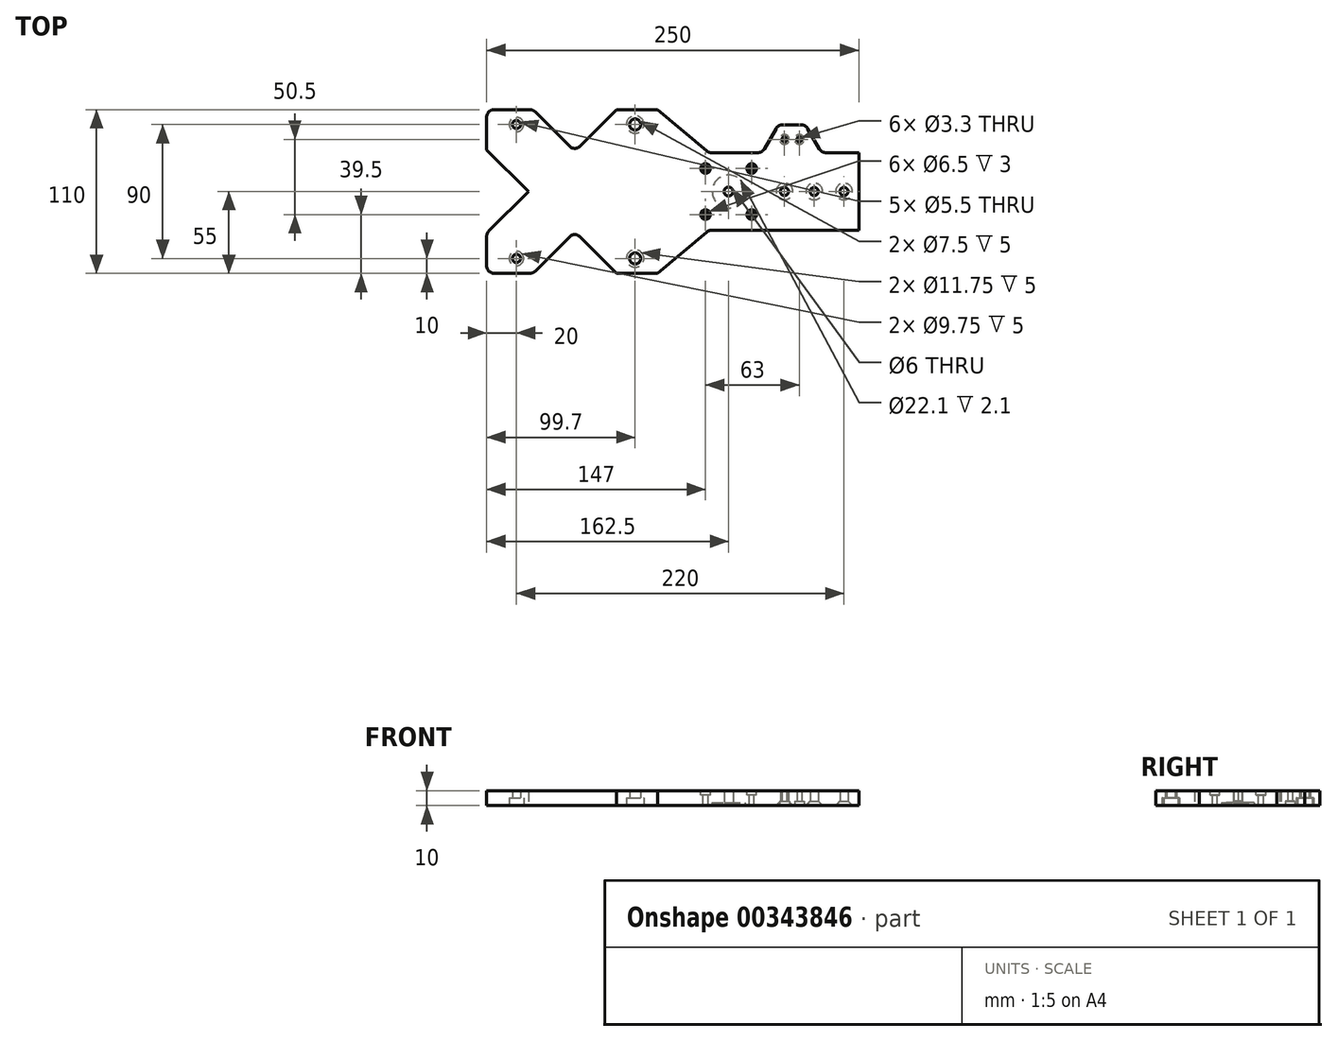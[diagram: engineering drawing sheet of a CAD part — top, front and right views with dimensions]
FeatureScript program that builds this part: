
annotation { "Feature Type Name" : "Feature", "Feature Type Description" : "" }
export const myFeature = defineFeature(function(context is Context, id is Id, definition is map)
    precondition{}
    {
        {
            var Q0;
            Q0=qCreatedBy(makeId("Top.planeOp"),FACE);
            var sketch = newSketch(context, id + "F0", { "sketchPlane" : qUnion([Q0])});
            skLineSegment(sketch, "E0.bottom", {"start": v(125, -55) * mm, "end": v(-125, -55) * mm});
            skLineSegment(sketch, "E0.top", {"start": v(125, 55) * mm, "end": v(-125, 55) * mm});
            skLineSegment(sketch, "E0.left", {"start": v(125, -55) * mm, "end": v(125, 55) * mm});
            skLineSegment(sketch, "E0.right", {"start": v(-125, -55) * mm, "end": v(-125, 55) * mm});
            skPoint(sketch, "E0.middle", {"position": v(0, 0) * mm});
            skCircle(sketch, "E1", {"center": v(-105, 45) * mm, "radius": 2.65 * mm});
            skCircle(sketch, "E2.MirrorC", {"center": v(-105, -45) * mm, "radius": 2.65 * mm});
            skCircle(sketch, "E3", {"center": v(-25.3, 45) * mm, "radius": 3.75 * mm});
            skCircle(sketch, "E4.MirrorC", {"center": v(-25.3, -45) * mm, "radius": 3.75 * mm});
            skCircle(sketch, "E5", {"center": v(115, 0) * mm, "radius": 2.65 * mm});
            skCircle(sketch, "E6", {"center": v(95, 0) * mm, "radius": 2.65 * mm});
            skCircle(sketch, "E7", {"center": v(75, 0) * mm, "radius": 2.65 * mm});
            skLineSegment(sketch, "E8", {"start": v(0, 0) * mm, "end": v(75, 0) * mm, "construction": true});
            skCircle(sketch, "E9", {"center": v(37.5, 0) * mm, "radius": 11.1 * mm, "construction": true});
            skLineSegment(sketch, "E10", {"start": v(37.5, 0) * mm, "end": v(22, -15.5) * mm, "construction": true});
            skLineSegment(sketch, "E11.MirrorCS", {"start": v(37.5, 0) * mm, "end": v(22, 15.5) * mm, "construction": true});
            skLineSegment(sketch, "E12", {"start": v(37.5, 38.01) * mm, "end": v(37.5, 0) * mm, "construction": true});
            skLineSegment(sketch, "E13.MirrorCS", {"start": v(37.5, 0) * mm, "end": v(53, -15.5) * mm, "construction": true});
            skLineSegment(sketch, "E14.MirrorCS", {"start": v(37.5, 0) * mm, "end": v(53, 15.5) * mm, "construction": true});
            skCircle(sketch, "E15", {"center": v(22, -15.5) * mm, "radius": 1.6 * mm});
            skCircle(sketch, "E16.MirrorC", {"center": v(53, -15.5) * mm, "radius": 1.6 * mm});
            skCircle(sketch, "E17.MirrorC", {"center": v(22, 15.5) * mm, "radius": 1.6 * mm});
            skCircle(sketch, "E18.MirrorC", {"center": v(53, 15.5) * mm, "radius": 1.6 * mm});
            skCircle(sketch, "E19", {"center": v(37.5, 0) * mm, "radius": 3 * mm});
            skLineSegment(sketch, "E20", {"start": v(-125, -28) * mm, "end": v(-97, 0) * mm});
            skLineSegment(sketch, "E21.MirrorCS", {"start": v(-125, 28) * mm, "end": v(-97, 0) * mm});
            skLineSegment(sketch, "E22", {"start": v(-125, 28) * mm, "end": v(-125, -28) * mm});
            skCircle(sketch, "E23", {"center": v(75, 35) * mm, "radius": 1.6 * mm});
            skCircle(sketch, "E24", {"center": v(85, 35) * mm, "radius": 1.6 * mm});
            skLineSegment(sketch, "E25", {"start": v(75, 35) * mm, "end": v(79.22, 35) * mm, "construction": true});
            skLineSegment(sketch, "E26", {"start": v(75, 68.62) * mm, "end": v(75, -17.42) * mm, "construction": true});
            skSolve(sketch);
        }
        {
            var Q0;
            Q0=qSketchRegion(id+"F0",true);
            extrude(context, id + "F1", {"entities" : qUnion([Q0]), "depth" : 10 * mm});
        }
        {
            var Q0;
            Q0=sQuery(id+"F0.wireOp",VERTEX,"E7.center");
            var Q1;
            Q1=sQuery(id+"F0.wireOp",VERTEX,"E6.center");
            var Q2;
            Q2=sQuery(id+"F0.wireOp",VERTEX,"E5.center");
            var Q3;
            Q3=makeQuery(id+"F1.opExtrude","SWEPT_BODY",BODY,{"disambiguationData":[OSD([sQuery(id+"F0.wireOp",EDGE,"E0.bottom"),sQuery(id+"F0.wireOp",EDGE,"E0.top"),sQuery(id+"F0.wireOp",EDGE,"E0.left"),sQuery(id+"F0.wireOp",EDGE,"E0.right"),sQuery(id+"F0.wireOp",EDGE,"E1"),sQuery(id+"F0.wireOp",EDGE,"E2.MirrorC"),sQuery(id+"F0.wireOp",EDGE,"E3"),sQuery(id+"F0.wireOp",EDGE,"E4.MirrorC"),sQuery(id+"F0.wireOp",EDGE,"E5"),sQuery(id+"F0.wireOp",EDGE,"E6"),sQuery(id+"F0.wireOp",EDGE,"E7")])]});
            hole(context, id + "F2", {"style" : HoleStyle.C_SINK, "endStyle" : HoleEndStyle.THROUGH, "oppositeDirection" : true, "standardTappedOrClearance" : lookupTablePath({ "standard" : "ISO", "fit" : "Normal", "size" : "M5", "type" : "Clearance" }), "standardBlindInLast" : lookupTablePath({ "fit" : "Standard", "standard" : "ISO", "size" : "M5", "type" : "Clearance" }), "holeDiameter" : 5.5 * mm, "cSinkDiameter" : 11.2 * mm, "cSinkAngle" : 90 * degree, "isTappedThrough" : true, "tappedDepth" : 12 * mm, "tapClearance" : 3, "locations" : qUnion([Q0, Q1, Q2]), "scope" : qUnion([Q3])});
        }
        {
            var Q0;
            Q0=sQuery(id+"F0.wireOp",VERTEX,"E14.MirrorCS.start");
            var Q1;
            Q1=makeQuery(id+"F1.opExtrude","SWEPT_BODY",BODY,{"disambiguationData":[OSD([sQuery(id+"F0.wireOp",EDGE,"E0.bottom"),sQuery(id+"F0.wireOp",EDGE,"E0.top"),sQuery(id+"F0.wireOp",EDGE,"E0.left"),sQuery(id+"F0.wireOp",EDGE,"E0.right"),sQuery(id+"F0.wireOp",EDGE,"E1"),sQuery(id+"F0.wireOp",EDGE,"E2.MirrorC"),sQuery(id+"F0.wireOp",EDGE,"E3"),sQuery(id+"F0.wireOp",EDGE,"E4.MirrorC"),sQuery(id+"F0.wireOp",EDGE,"E5"),sQuery(id+"F0.wireOp",EDGE,"E6"),sQuery(id+"F0.wireOp",EDGE,"E7"),sQuery(id+"F0.wireOp",EDGE,"E15"),sQuery(id+"F0.wireOp",EDGE,"E16.MirrorC"),sQuery(id+"F0.wireOp",EDGE,"E17.MirrorC"),sQuery(id+"F0.wireOp",EDGE,"E18.MirrorC"),sQuery(id+"F0.wireOp",EDGE,"E19")])]});
            hole(context, id + "F3", {"style" : HoleStyle.C_BORE, "endStyle" : HoleEndStyle.THROUGH, "oppositeDirection" : true, "holeDiameter" : 5.5 * mm, "cBoreDiameter" : 22.1 * mm, "cBoreDepth" : 2.1 * mm, "isTappedThrough" : true, "tappedDepth" : 12 * mm, "tapClearance" : 3, "locations" : qUnion([Q0]), "scope" : qUnion([Q1])});
        }
        {
            var Q0;
            Q0=makeQuery(id+"F0.imprint","IMPRINT",FACE,{"disambiguationData":[TD([[makeQuery(id+"F0.imprint","IMPRINT",EDGE,{"derivedFrom":sQuery(id+"F0.wireOp",EDGE,"E20")}),1.0]])]});
            extrude(context, id + "F4", {"entities" : qUnion([Q0]), "operationType" : NewBodyOperationType.REMOVE, "endBound" : BoundingType.THROUGH_ALL, "depth" : 25 * mm});
        }
        {
            var Q0;
            Q0=sQuery(id+"F0.wireOp",VERTEX,"E23.center");
            var Q1;
            Q1=sQuery(id+"F0.wireOp",VERTEX,"E24.center");
            var Q2;
            Q2=makeQuery(id+"F1.opExtrude","SWEPT_BODY",BODY,{"disambiguationData":[OSD([sQuery(id+"F0.wireOp",EDGE,"E0.bottom"),sQuery(id+"F0.wireOp",EDGE,"E0.top"),sQuery(id+"F0.wireOp",EDGE,"E0.left"),sQuery(id+"F0.wireOp",EDGE,"E0.right"),sQuery(id+"F0.wireOp",EDGE,"E1"),sQuery(id+"F0.wireOp",EDGE,"E2.MirrorC"),sQuery(id+"F0.wireOp",EDGE,"E3"),sQuery(id+"F0.wireOp",EDGE,"E4.MirrorC"),sQuery(id+"F0.wireOp",EDGE,"E5"),sQuery(id+"F0.wireOp",EDGE,"E6"),sQuery(id+"F0.wireOp",EDGE,"E7"),sQuery(id+"F0.wireOp",EDGE,"E15"),sQuery(id+"F0.wireOp",EDGE,"E16.MirrorC"),sQuery(id+"F0.wireOp",EDGE,"E17.MirrorC"),sQuery(id+"F0.wireOp",EDGE,"E18.MirrorC"),sQuery(id+"F0.wireOp",EDGE,"E19"),sQuery(id+"F0.wireOp",EDGE,"E22")])]});
            hole(context, id + "F5", {"style" : HoleStyle.C_BORE, "endStyle" : HoleEndStyle.THROUGH, "oppositeDirection" : true, "standardTappedOrClearance" : lookupTablePath({ "standard" : "ISO", "fit" : "Normal", "size" : "M3", "type" : "Clearance" }), "standardBlindInLast" : lookupTablePath({ "fit" : "Standard", "standard" : "ISO", "size" : "M3", "type" : "Clearance" }), "holeDiameter" : 3.3 * mm, "cBoreDiameter" : 6.5 * mm, "cBoreDepth" : 3 * mm, "isTappedThrough" : true, "tappedDepth" : 12 * mm, "tapClearance" : 3, "locations" : qUnion([Q0, Q1]), "scope" : qUnion([Q2])});
        }
        {
            var Q0;
            Q0=sQuery(id+"F0.wireOp",VERTEX,"E4.MirrorC.center");
            var Q1;
            Q1=sQuery(id+"F0.wireOp",VERTEX,"E3.center");
            var Q2;
            Q2=makeQuery(id+"F1.opExtrude","SWEPT_BODY",BODY,{"disambiguationData":[OSD([sQuery(id+"F0.wireOp",EDGE,"E0.bottom"),sQuery(id+"F0.wireOp",EDGE,"E0.top"),sQuery(id+"F0.wireOp",EDGE,"E0.left"),sQuery(id+"F0.wireOp",EDGE,"E0.right"),sQuery(id+"F0.wireOp",EDGE,"E1"),sQuery(id+"F0.wireOp",EDGE,"E2.MirrorC"),sQuery(id+"F0.wireOp",EDGE,"E3"),sQuery(id+"F0.wireOp",EDGE,"E4.MirrorC"),sQuery(id+"F0.wireOp",EDGE,"E5"),sQuery(id+"F0.wireOp",EDGE,"E6"),sQuery(id+"F0.wireOp",EDGE,"E7"),sQuery(id+"F0.wireOp",EDGE,"E15"),sQuery(id+"F0.wireOp",EDGE,"E16.MirrorC"),sQuery(id+"F0.wireOp",EDGE,"E17.MirrorC"),sQuery(id+"F0.wireOp",EDGE,"E18.MirrorC"),sQuery(id+"F0.wireOp",EDGE,"E19"),sQuery(id+"F0.wireOp",EDGE,"E22")])]});
            hole(context, id + "F6", {"style" : HoleStyle.C_BORE, "endStyle" : HoleEndStyle.THROUGH, "oppositeDirection" : true, "holeDiameter" : 7.5 * mm, "cBoreDiameter" : 11.75 * mm, "cBoreDepth" : 5 * mm, "isTappedThrough" : true, "tappedDepth" : 12 * mm, "tapClearance" : 3, "locations" : qUnion([Q0, Q1]), "scope" : qUnion([Q2])});
        }
        {
            var Q0;
            Q0=makeQuery(id+"F1.opExtrude","CAP_FACE",FACE,{"disambiguationData":[OSD([sQuery(id+"F0.wireOp",EDGE,"E0.bottom"),sQuery(id+"F0.wireOp",EDGE,"E0.top"),sQuery(id+"F0.wireOp",EDGE,"E0.left"),sQuery(id+"F0.wireOp",EDGE,"E0.right"),sQuery(id+"F0.wireOp",EDGE,"E1"),sQuery(id+"F0.wireOp",EDGE,"E2.MirrorC"),sQuery(id+"F0.wireOp",EDGE,"E3"),sQuery(id+"F0.wireOp",EDGE,"E4.MirrorC"),sQuery(id+"F0.wireOp",EDGE,"E5"),sQuery(id+"F0.wireOp",EDGE,"E6"),sQuery(id+"F0.wireOp",EDGE,"E7"),sQuery(id+"F0.wireOp",EDGE,"E15"),sQuery(id+"F0.wireOp",EDGE,"E16.MirrorC"),sQuery(id+"F0.wireOp",EDGE,"E17.MirrorC"),sQuery(id+"F0.wireOp",EDGE,"E18.MirrorC"),sQuery(id+"F0.wireOp",EDGE,"E19"),sQuery(id+"F0.wireOp",EDGE,"E22"),sQuery(id+"F0.wireOp",EDGE,"E23"),sQuery(id+"F0.wireOp",EDGE,"E24")])],"isStart":false});
            cPlane(context, id + "F7", {"entities" : qUnion([Q0]), "cplaneType" : CPlaneType.OFFSET, "offset" : 0 * mm, "width" : 150 * mm, "height" : 150 * mm});
        }
        {
            var Q0;
            Q0=qCreatedBy(id+"F7.planeOp",FACE);
            var sketch = newSketch(context, id + "F8", { "sketchPlane" : qUnion([Q0])});
            skCircle(sketch, "E27.0", {"center": v(22, 15.5) * mm, "radius": 1.6 * mm, "construction": true});
            skCircle(sketch, "E27.1", {"center": v(53, 15.5) * mm, "radius": 1.6 * mm, "construction": true});
            skCircle(sketch, "E27.2", {"center": v(53, -15.5) * mm, "radius": 1.6 * mm, "construction": true});
            skCircle(sketch, "E27.3", {"center": v(22, -15.5) * mm, "radius": 1.6 * mm, "construction": true});
            skSolve(sketch);
        }
        {
            var Q0;
            Q0=sQuery(id+"F8.wireOp",VERTEX,"E27.1.center");
            var Q1;
            Q1=sQuery(id+"F8.wireOp",VERTEX,"E27.2.center");
            var Q2;
            Q2=sQuery(id+"F8.wireOp",VERTEX,"E27.3.center");
            var Q3;
            Q3=sQuery(id+"F8.wireOp",VERTEX,"E27.0.center");
            var Q4;
            Q4=makeQuery(id+"F1.opExtrude","SWEPT_BODY",BODY,{"disambiguationData":[OSD([sQuery(id+"F0.wireOp",EDGE,"E0.bottom"),sQuery(id+"F0.wireOp",EDGE,"E0.top"),sQuery(id+"F0.wireOp",EDGE,"E0.left"),sQuery(id+"F0.wireOp",EDGE,"E0.right"),sQuery(id+"F0.wireOp",EDGE,"E1"),sQuery(id+"F0.wireOp",EDGE,"E2.MirrorC"),sQuery(id+"F0.wireOp",EDGE,"E3"),sQuery(id+"F0.wireOp",EDGE,"E4.MirrorC"),sQuery(id+"F0.wireOp",EDGE,"E5"),sQuery(id+"F0.wireOp",EDGE,"E6"),sQuery(id+"F0.wireOp",EDGE,"E7"),sQuery(id+"F0.wireOp",EDGE,"E15"),sQuery(id+"F0.wireOp",EDGE,"E16.MirrorC"),sQuery(id+"F0.wireOp",EDGE,"E17.MirrorC"),sQuery(id+"F0.wireOp",EDGE,"E18.MirrorC"),sQuery(id+"F0.wireOp",EDGE,"E19"),sQuery(id+"F0.wireOp",EDGE,"E22"),sQuery(id+"F0.wireOp",EDGE,"E23"),sQuery(id+"F0.wireOp",EDGE,"E24")])]});
            hole(context, id + "F9", {"style" : HoleStyle.C_BORE, "endStyle" : HoleEndStyle.THROUGH, "standardTappedOrClearance" : lookupTablePath({ "standard" : "ISO", "fit" : "Normal", "size" : "M3", "type" : "Clearance" }), "standardBlindInLast" : lookupTablePath({ "fit" : "Standard", "standard" : "ISO", "size" : "M3", "type" : "Clearance" }), "holeDiameter" : 3.3 * mm, "cBoreDiameter" : 6.5 * mm, "cBoreDepth" : 3 * mm, "isTappedThrough" : true, "tappedDepth" : 12 * mm, "tapClearance" : 3, "locations" : qUnion([Q0, Q1, Q2, Q3]), "scope" : qUnion([Q4])});
        }
        {
            var Q0;
            Q0=sQuery(id+"F0.wireOp",VERTEX,"E2.MirrorC.center");
            var Q1;
            Q1=sQuery(id+"F0.wireOp",VERTEX,"E1.center");
            var Q2;
            Q2=makeQuery(id+"F1.opExtrude","SWEPT_BODY",BODY,{"disambiguationData":[OSD([sQuery(id+"F0.wireOp",EDGE,"E0.bottom"),sQuery(id+"F0.wireOp",EDGE,"E0.top"),sQuery(id+"F0.wireOp",EDGE,"E0.left"),sQuery(id+"F0.wireOp",EDGE,"E0.right"),sQuery(id+"F0.wireOp",EDGE,"E1"),sQuery(id+"F0.wireOp",EDGE,"E2.MirrorC"),sQuery(id+"F0.wireOp",EDGE,"E3"),sQuery(id+"F0.wireOp",EDGE,"E4.MirrorC"),sQuery(id+"F0.wireOp",EDGE,"E5"),sQuery(id+"F0.wireOp",EDGE,"E6"),sQuery(id+"F0.wireOp",EDGE,"E7"),sQuery(id+"F0.wireOp",EDGE,"E15"),sQuery(id+"F0.wireOp",EDGE,"E16.MirrorC"),sQuery(id+"F0.wireOp",EDGE,"E17.MirrorC"),sQuery(id+"F0.wireOp",EDGE,"E18.MirrorC"),sQuery(id+"F0.wireOp",EDGE,"E19"),sQuery(id+"F0.wireOp",EDGE,"E22"),sQuery(id+"F0.wireOp",EDGE,"E23"),sQuery(id+"F0.wireOp",EDGE,"E24")])]});
            hole(context, id + "F10", {"style" : HoleStyle.C_BORE, "endStyle" : HoleEndStyle.THROUGH, "oppositeDirection" : true, "standardTappedOrClearance" : lookupTablePath({ "standard" : "ISO", "fit" : "Normal", "size" : "M5", "type" : "Clearance" }), "standardBlindInLast" : lookupTablePath({ "fit" : "Standard", "standard" : "ISO", "size" : "M5", "type" : "Clearance" }), "holeDiameter" : 5.5 * mm, "cBoreDiameter" : 9.75 * mm, "cBoreDepth" : 5 * mm, "isTappedThrough" : true, "tappedDepth" : 12 * mm, "tapClearance" : 3, "locations" : qUnion([Q0, Q1]), "scope" : qUnion([Q2])});
        }
        {
            var Q0;
            Q0=qCreatedBy(id+"F7.planeOp",FACE);
            var sketch = newSketch(context, id + "F11", { "sketchPlane" : qUnion([Q0])});
            skLineSegment(sketch, "E28.0.0", {"start": v(-125, 55) * mm, "end": v(-125, 28) * mm});
            skLineSegment(sketch, "E28.0.1", {"start": v(-125, 28) * mm, "end": v(-97, 0) * mm});
            skLineSegment(sketch, "E28.0.2", {"start": v(-97, 0) * mm, "end": v(-125, -28) * mm});
            skLineSegment(sketch, "E28.0.3", {"start": v(-125, -28) * mm, "end": v(-125, -55) * mm});
            skLineSegment(sketch, "E28.0.4", {"start": v(-125, -55) * mm, "end": v(125, -55) * mm});
            skLineSegment(sketch, "E28.0.5", {"start": v(125, -55) * mm, "end": v(125, 55) * mm});
            skLineSegment(sketch, "E28.0.6", {"start": v(125, 55) * mm, "end": v(-125, 55) * mm});
            skLineSegment(sketch, "E29", {"start": v(-10.3, -55) * mm, "end": v(24.17, -26.07) * mm});
            skLineSegment(sketch, "E30", {"start": v(24.17, -26.07) * mm, "end": v(125, -26.07) * mm});
            skLineSegment(sketch, "E31.MirrorCS", {"start": v(-10.3, 55) * mm, "end": v(24.17, 26.07) * mm});
            skLineSegment(sketch, "E32.MirrorCS", {"start": v(24.17, 26.07) * mm, "end": v(125, 26.07) * mm});
            skLineSegment(sketch, "E33", {"start": v(60, 26.07) * mm, "end": v(70.83, 44.83) * mm});
            skLineSegment(sketch, "E34", {"start": v(70.83, 44.83) * mm, "end": v(89.17, 44.83) * mm});
            skLineSegment(sketch, "E35", {"start": v(89.17, 44.83) * mm, "end": v(100, 26.07) * mm});
            skLineSegment(sketch, "E36", {"start": v(-93.96, -55) * mm, "end": v(-65.86, -26.9) * mm});
            skLineSegment(sketch, "E37", {"start": v(-65.86, -26.9) * mm, "end": v(-37.75, -55) * mm});
            skLineSegment(sketch, "E38", {"start": v(-97, 0) * mm, "end": v(0, 0) * mm, "construction": true});
            skLineSegment(sketch, "E39.MirrorCS", {"start": v(-65.86, 26.9) * mm, "end": v(-37.75, 55) * mm});
            skLineSegment(sketch, "E40.MirrorCS", {"start": v(-93.96, 55) * mm, "end": v(-65.86, 26.9) * mm});
            skSolve(sketch);
        }
        {
            var Q0;
            {var subQ1=sQuery(id+"F11.wireOp",EDGE,"E31.MirrorCS");Q0=makeQuery(id+"F11.imprint","IMPRINT",FACE,{"disambiguationData":[TD([[makeQuery(id+"F11.imprint","IMPRINT",EDGE,{"derivedFrom":subQ1}),1.0]])]});}
            var Q1;
            {var subQ3=sQuery(id+"F11.wireOp",EDGE,"E29");Q1=makeQuery(id+"F11.imprint","IMPRINT",FACE,{"disambiguationData":[TD([[makeQuery(id+"F11.imprint","IMPRINT",EDGE,{"derivedFrom":subQ3}),-1.0]])]});}
            var Q2;
            {var subQ0=sQuery(id+"F11.wireOp",EDGE,"E36");Q2=makeQuery(id+"F11.imprint","IMPRINT",FACE,{"disambiguationData":[TD([[makeQuery(id+"F11.imprint","IMPRINT",EDGE,{"derivedFrom":subQ0}),-1.0]])]});}
            var Q3;
            {var subQ0=sQuery(id+"F11.wireOp",EDGE,"E39.MirrorCS");Q3=makeQuery(id+"F11.imprint","IMPRINT",FACE,{"disambiguationData":[TD([[makeQuery(id+"F11.imprint","IMPRINT",EDGE,{"derivedFrom":subQ0}),1.0]])]});}
            extrude(context, id + "F12", {"entities" : qUnion([Q0, Q1, Q2, Q3]), "operationType" : NewBodyOperationType.REMOVE, "oppositeDirection" : true, "depth" : 25 * mm, "offsetDistance" : 25 * mm});
        }
        {
            var Q0;
            Q0=makeQuery(id+"F4.boolean.opBoolean","COPY",EDGE,{"derivedFrom":makeQuery(id+"F4.opExtrude","SWEPT_EDGE",EDGE,{"disambiguationData":[OSD([sQuery(id+"F0.wireOp",EDGE,"E0.right"),sQuery(id+"F0.wireOp",EDGE,"E20"),sQuery(id+"F0.wireOp",EDGE,"E22")])]})});
            var Q1;
            Q1=makeQuery(id+"F1.opExtrude","SWEPT_EDGE",EDGE,{"disambiguationData":[OSD([sQuery(id+"F0.wireOp",EDGE,"E0.bottom"),sQuery(id+"F0.wireOp",EDGE,"E0.right")])]});
            var Q2;
            Q2=makeQuery(id+"F4.boolean.opBoolean","COPY",EDGE,{"derivedFrom":makeQuery(id+"F4.opExtrude","SWEPT_EDGE",EDGE,{"disambiguationData":[OSD([sQuery(id+"F0.wireOp",EDGE,"E0.right"),sQuery(id+"F0.wireOp",EDGE,"E21.MirrorCS"),sQuery(id+"F0.wireOp",EDGE,"E22")])]})});
            var Q3;
            Q3=makeQuery(id+"F1.opExtrude","SWEPT_EDGE",EDGE,{"disambiguationData":[OSD([sQuery(id+"F0.wireOp",EDGE,"E0.top"),sQuery(id+"F0.wireOp",EDGE,"E0.right")])]});
            var Q4;
            Q4=makeQuery(id+"F12.boolean.opBoolean","COPY",EDGE,{"derivedFrom":makeQuery(id+"F12.opExtrude","SWEPT_EDGE",EDGE,{"disambiguationData":[OSD([sQuery(id+"F11.wireOp",EDGE,"E29"),sQuery(id+"F11.wireOp",EDGE,"E30")])]})});
            var Q5;
            Q5=makeQuery(id+"F12.boolean.opBoolean","COPY",EDGE,{"derivedFrom":makeQuery(id+"F12.opExtrude","SWEPT_EDGE",EDGE,{"disambiguationData":[OSD([sQuery(id+"F11.wireOp",EDGE,"E28.0.4"),sQuery(id+"F11.wireOp",EDGE,"E29")])]})});
            var Q6;
            Q6=makeQuery(id+"F12.boolean.opBoolean","COPY",EDGE,{"derivedFrom":makeQuery(id+"F12.opExtrude","SWEPT_EDGE",EDGE,{"disambiguationData":[OSD([sQuery(id+"F11.wireOp",EDGE,"E28.0.5"),sQuery(id+"F11.wireOp",EDGE,"E30")])]})});
            var Q7;
            Q7=makeQuery(id+"F12.boolean.opBoolean","COPY",EDGE,{"derivedFrom":makeQuery(id+"F12.opExtrude","SWEPT_EDGE",EDGE,{"disambiguationData":[OSD([sQuery(id+"F11.wireOp",EDGE,"E28.0.5"),sQuery(id+"F11.wireOp",EDGE,"E32.MirrorCS")])]})});
            var Q8;
            Q8=makeQuery(id+"F12.boolean.opBoolean","COPY",EDGE,{"derivedFrom":makeQuery(id+"F12.opExtrude","SWEPT_EDGE",EDGE,{"disambiguationData":[OSD([sQuery(id+"F11.wireOp",EDGE,"E32.MirrorCS"),sQuery(id+"F11.wireOp",EDGE,"E35")])]})});
            var Q9;
            Q9=makeQuery(id+"F12.boolean.opBoolean","COPY",EDGE,{"derivedFrom":makeQuery(id+"F12.opExtrude","SWEPT_EDGE",EDGE,{"disambiguationData":[OSD([sQuery(id+"F11.wireOp",EDGE,"E34"),sQuery(id+"F11.wireOp",EDGE,"E35")])]})});
            var Q10;
            Q10=makeQuery(id+"F12.boolean.opBoolean","COPY",EDGE,{"derivedFrom":makeQuery(id+"F12.opExtrude","SWEPT_EDGE",EDGE,{"disambiguationData":[OSD([sQuery(id+"F11.wireOp",EDGE,"E33"),sQuery(id+"F11.wireOp",EDGE,"E34")])]})});
            var Q11;
            Q11=makeQuery(id+"F12.boolean.opBoolean","COPY",EDGE,{"derivedFrom":makeQuery(id+"F12.opExtrude","SWEPT_EDGE",EDGE,{"disambiguationData":[OSD([sQuery(id+"F11.wireOp",EDGE,"E32.MirrorCS"),sQuery(id+"F11.wireOp",EDGE,"E33")])]})});
            var Q12;
            Q12=makeQuery(id+"F12.boolean.opBoolean","COPY",EDGE,{"derivedFrom":makeQuery(id+"F12.opExtrude","SWEPT_EDGE",EDGE,{"disambiguationData":[OSD([sQuery(id+"F11.wireOp",EDGE,"E31.MirrorCS"),sQuery(id+"F11.wireOp",EDGE,"E32.MirrorCS")])]})});
            var Q13;
            Q13=makeQuery(id+"F12.boolean.opBoolean","COPY",EDGE,{"derivedFrom":makeQuery(id+"F12.opExtrude","SWEPT_EDGE",EDGE,{"disambiguationData":[OSD([sQuery(id+"F11.wireOp",EDGE,"E28.0.6"),sQuery(id+"F11.wireOp",EDGE,"E31.MirrorCS")])]})});
            var Q14;
            Q14=makeQuery(id+"F12.boolean.opBoolean","COPY",EDGE,{"derivedFrom":makeQuery(id+"F12.opExtrude","SWEPT_EDGE",EDGE,{"disambiguationData":[OSD([sQuery(id+"F11.wireOp",EDGE,"E36"),sQuery(id+"F11.wireOp",EDGE,"E37")])]})});
            var Q15;
            Q15=makeQuery(id+"F12.boolean.opBoolean","COPY",EDGE,{"derivedFrom":makeQuery(id+"F12.opExtrude","SWEPT_EDGE",EDGE,{"disambiguationData":[OSD([sQuery(id+"F11.wireOp",EDGE,"E39.MirrorCS"),sQuery(id+"F11.wireOp",EDGE,"E40.MirrorCS")])]})});
            var Q16;
            Q16=makeQuery(id+"F12.boolean.opBoolean","COPY",EDGE,{"derivedFrom":makeQuery(id+"F12.opExtrude","SWEPT_EDGE",EDGE,{"disambiguationData":[OSD([sQuery(id+"F11.wireOp",EDGE,"E28.0.4"),sQuery(id+"F11.wireOp",EDGE,"E36")])]})});
            var Q17;
            Q17=makeQuery(id+"F12.boolean.opBoolean","COPY",EDGE,{"derivedFrom":makeQuery(id+"F12.opExtrude","SWEPT_EDGE",EDGE,{"disambiguationData":[OSD([sQuery(id+"F11.wireOp",EDGE,"E28.0.4"),sQuery(id+"F11.wireOp",EDGE,"E37")])]})});
            var Q18;
            Q18=makeQuery(id+"F12.boolean.opBoolean","COPY",EDGE,{"derivedFrom":makeQuery(id+"F12.opExtrude","SWEPT_EDGE",EDGE,{"disambiguationData":[OSD([sQuery(id+"F11.wireOp",EDGE,"E28.0.6"),sQuery(id+"F11.wireOp",EDGE,"E39.MirrorCS")])]})});
            var Q19;
            Q19=makeQuery(id+"F12.boolean.opBoolean","COPY",EDGE,{"derivedFrom":makeQuery(id+"F12.opExtrude","SWEPT_EDGE",EDGE,{"disambiguationData":[OSD([sQuery(id+"F11.wireOp",EDGE,"E28.0.6"),sQuery(id+"F11.wireOp",EDGE,"E40.MirrorCS")])]})});
            fillet(context, id + "F13", {"entities" : qUnion([Q0, Q1, Q2, Q3, Q4, Q5, Q6, Q7, Q8, Q9, Q10, Q11, Q12, Q13, Q14, Q15, Q16, Q17, Q18, Q19]), "radius" : 5 * mm, "tangentPropagation" : true, "allowEdgeOverflow" : false});
        }
    });
